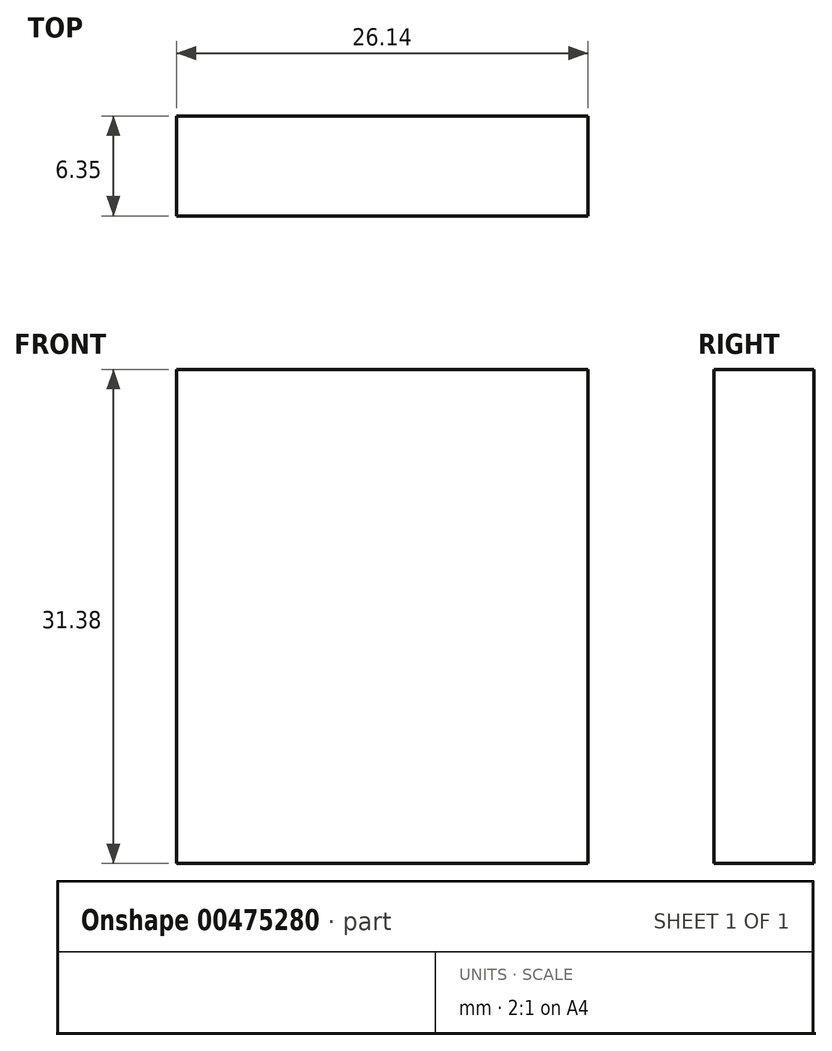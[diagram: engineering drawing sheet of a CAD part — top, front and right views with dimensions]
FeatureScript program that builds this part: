
annotation { "Feature Type Name" : "Feature", "Feature Type Description" : "" }
export const myFeature = defineFeature(function(context is Context, id is Id, definition is map)
    precondition{}
    {
        {
            var Q0;
            Q0=qCreatedBy(makeId("Front.planeOp"),FACE);
            var sketch = newSketch(context, id + "F0", { "sketchPlane" : qUnion([Q0])});
            skLineSegment(sketch, "E0", {"start": v(0, 0) * mm, "end": v(26.14, 0) * mm});
            skLineSegment(sketch, "E1", {"start": v(26.14, 0) * mm, "end": v(26.14, 31.38) * mm});
            skLineSegment(sketch, "E2", {"start": v(26.14, 31.38) * mm, "end": v(0, 31.38) * mm});
            skLineSegment(sketch, "E3", {"start": v(0, 31.38) * mm, "end": v(0, 0) * mm});
            skSolve(sketch);
        }
        {
            var Q0;
            Q0=makeQuery(id+"F0.imprint","IMPRINT",FACE,{"disambiguationData":[TD([[makeQuery(id+"F0.imprint","IMPRINT",EDGE,{"derivedFrom":sQuery(id+"F0.wireOp",EDGE,"E0")}),1.0]])]});
            extrude(context, id + "F1", {"entities" : qUnion([Q0]), "depth" : 6.35 * mm});
        }
    });
